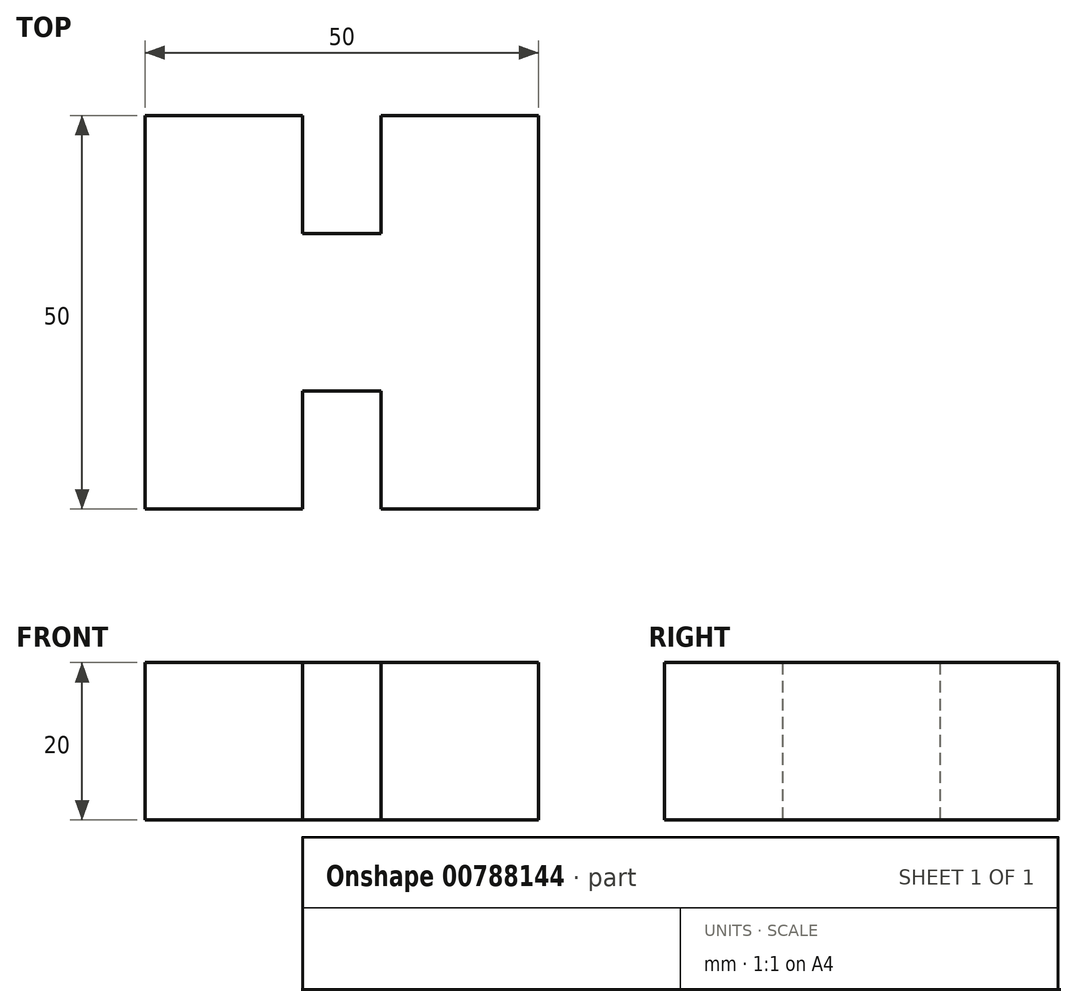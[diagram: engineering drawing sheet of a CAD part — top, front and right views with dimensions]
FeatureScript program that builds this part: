
annotation { "Feature Type Name" : "Feature", "Feature Type Description" : "" }
export const myFeature = defineFeature(function(context is Context, id is Id, definition is map)
    precondition{}
    {
        {
            var Q0;
            Q0=qCreatedBy(makeId("Top.planeOp"),FACE);
            var sketch = newSketch(context, id + "F0", { "sketchPlane" : qUnion([Q0])});
            skLineSegment(sketch, "E0", {"start": v(-59, 13.69) * mm, "end": v(-39, 13.69) * mm});
            skLineSegment(sketch, "E1", {"start": v(-39, 13.69) * mm, "end": v(-39, -1.31) * mm});
            skLineSegment(sketch, "E2", {"start": v(-39, -1.31) * mm, "end": v(-29, -1.31) * mm});
            skLineSegment(sketch, "E3", {"start": v(-29, -1.31) * mm, "end": v(-29, 13.69) * mm});
            skLineSegment(sketch, "E4", {"start": v(-29, 13.69) * mm, "end": v(-9, 13.69) * mm});
            skLineSegment(sketch, "E5", {"start": v(-9, 13.69) * mm, "end": v(-9, -36.31) * mm});
            skLineSegment(sketch, "E6", {"start": v(-9, -36.31) * mm, "end": v(-29, -36.31) * mm});
            skLineSegment(sketch, "E7", {"start": v(-29, -36.31) * mm, "end": v(-29, -21.31) * mm});
            skLineSegment(sketch, "E8", {"start": v(-29, -21.31) * mm, "end": v(-39, -21.31) * mm});
            skLineSegment(sketch, "E9", {"start": v(-39, -21.31) * mm, "end": v(-39, -36.31) * mm});
            skLineSegment(sketch, "E10", {"start": v(-39, -36.31) * mm, "end": v(-59, -36.31) * mm});
            skLineSegment(sketch, "E11", {"start": v(-59, -36.31) * mm, "end": v(-59, 13.69) * mm});
            skSolve(sketch);
        }
        {
            var Q0;
            Q0=makeQuery(id+"F0.imprint","IMPRINT",FACE,{"disambiguationData":[TD([[makeQuery(id+"F0.imprint","IMPRINT",EDGE,{"derivedFrom":sQuery(id+"F0.wireOp",EDGE,"E0")}),-1.0]])]});
            extrude(context, id + "F1", {"entities" : qUnion([Q0]), "depth" : 20 * mm, "offsetDistance" : 25 * mm});
        }
    });
